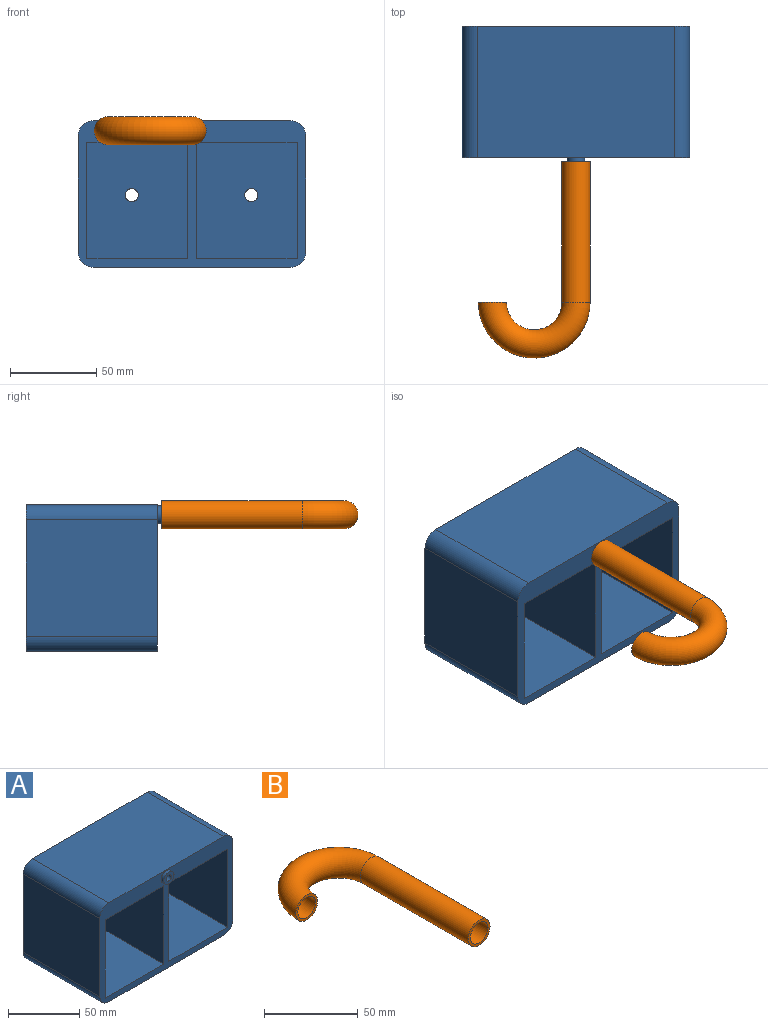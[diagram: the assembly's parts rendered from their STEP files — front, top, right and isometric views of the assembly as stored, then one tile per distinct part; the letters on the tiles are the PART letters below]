
ASSEMBLY  parts=2 mates=1
PART A: 25 faces, bbox 132.1x78.7x85.1 mm
  f0: plane 114.27x76.2mm, normal (0,0,-1), area 8707.4mm2, adj f12,f13,f16,f19
  f1: plane 76.2x67.36mm, normal (1,0,0), area 5132.8mm2, adj f12,f13,f16,f17
  f2: plane 114.27x76.2mm, normal (0,0,1), area 8707.4mm2, adj f12,f13,f17,f18
  f3: plane 63.5x58.41mm, normal (0,0,1), area 3708.7mm2, adj f4,f9,f12,f14
  f4: plane 67.36x63.5mm, normal (1,0,0), area 4277.4mm2, adj f3,f5,f12,f14
  f5: plane 63.5x58.41mm, normal (0,0,-1), area 3708.7mm2, adj f4,f9,f12,f14
  f6: plane 63.5x58.41mm, normal (0,0,1), area 3708.7mm2, adj f7,f10,f12,f15
  f7: plane 67.36x63.5mm, normal (1,0,0), area 4277.4mm2, adj f6,f8,f12,f15
  f8: plane 63.5x58.41mm, normal (0,0,-1), area 3708.7mm2, adj f7,f10,f12,f15
  f9: plane 67.36x63.5mm, normal (-1,0,0), area 4277.4mm2, adj f3,f5,f12,f14
  f10: plane 67.36x63.5mm, normal (-1,0,0), area 4277.4mm2, adj f6,f8,f12,f15
  f11: plane 76.2x67.36mm, normal (-1,0,0), area 5132.8mm2, adj f12,f13,f18,f19
  f12: plane 132.05x85.14mm, normal (0,-1,0), area 3225.5mm2, adj f0,f1,f2,f3,f4,f5,f6,f7
  f13: plane 132.05x85.14mm, normal (0,1,0), area 11063.5mm2, adj f0,f1,f2,f11,f16,f17,f18,f19
  f14: plane 67.36x58.41mm, normal (0,-1,0), area 3888.6mm2, adj f3,f4,f5,f9,f21
  f15: plane 67.36x58.41mm, normal (0,-1,0), area 3888.6mm2, adj f6,f7,f8,f10,f20
  f16: cylinder r=8.89mm len=76.2mm, axis (0,1,0), area 1064.1mm2, adj f0,f1,f12,f13
  f17: cylinder r=8.89mm len=76.2mm, axis (0,-1,0), area 1064.1mm2, adj f1,f2,f12,f13
  f18: cylinder r=8.89mm len=76.2mm, axis (0,1,0), area 1064.1mm2, adj f2,f11,f12,f13
  f19: cylinder r=8.89mm len=76.2mm, axis (0,-1,0), area 1064.1mm2, adj f0,f11,f12,f13
  f20: cylinder r=3.81mm len=12.7mm, axis (0,-1,0), area 304mm2, adj f13,f15
  f21: cylinder r=3.81mm len=12.7mm, axis (0,-1,0), area 304mm2, adj f13,f14
  f22: cylinder r=2.54mm len=78.74mm, axis (0,-1,0), area 1256.6mm2, adj f13,f24
  f23: cylinder r=5.08mm len=10.16mm, axis (0,1,0), area 81.1mm2, adj f12,f24
  f24: plane 10.16x10.16mm, normal (0,-1,0), area 60.8mm2, adj f22,f23
PART B: 6 faces, bbox 70.2x116.5x16.4 mm
  f0: cylinder r=6.68mm len=81.43mm, axis (0,1,0), area 3419.5mm2, adj f1,f2
  f1: torus R=24.24mm, axis (0,0,1), area 3198.3mm2, adj f0,f3
  f2: plane 16.37x16.37mm, normal (0,-1,0), area 70.2mm2, adj f0,f4
  f3: plane 16.37x16.37mm, normal (0,-1,0), area 70.2mm2, adj f1,f5
  f4: cylinder r=8.19mm len=81.43mm, axis (0,1,0), area 4188.6mm2, adj f2,f5
  f5: torus R=24.24mm, axis (0,0,1), area 3917.7mm2, adj f3,f4
PLACE A t=(-22.8,17.17,-11.65)mm
PLACE B rot(axis=(1,0,0),180deg) t=(-22.8,-61.57,25.08)mm
MATE revolute B.f0 <-> A.f22  axis (0,1,0) through (-22.8,-61.57,25.08)mm
